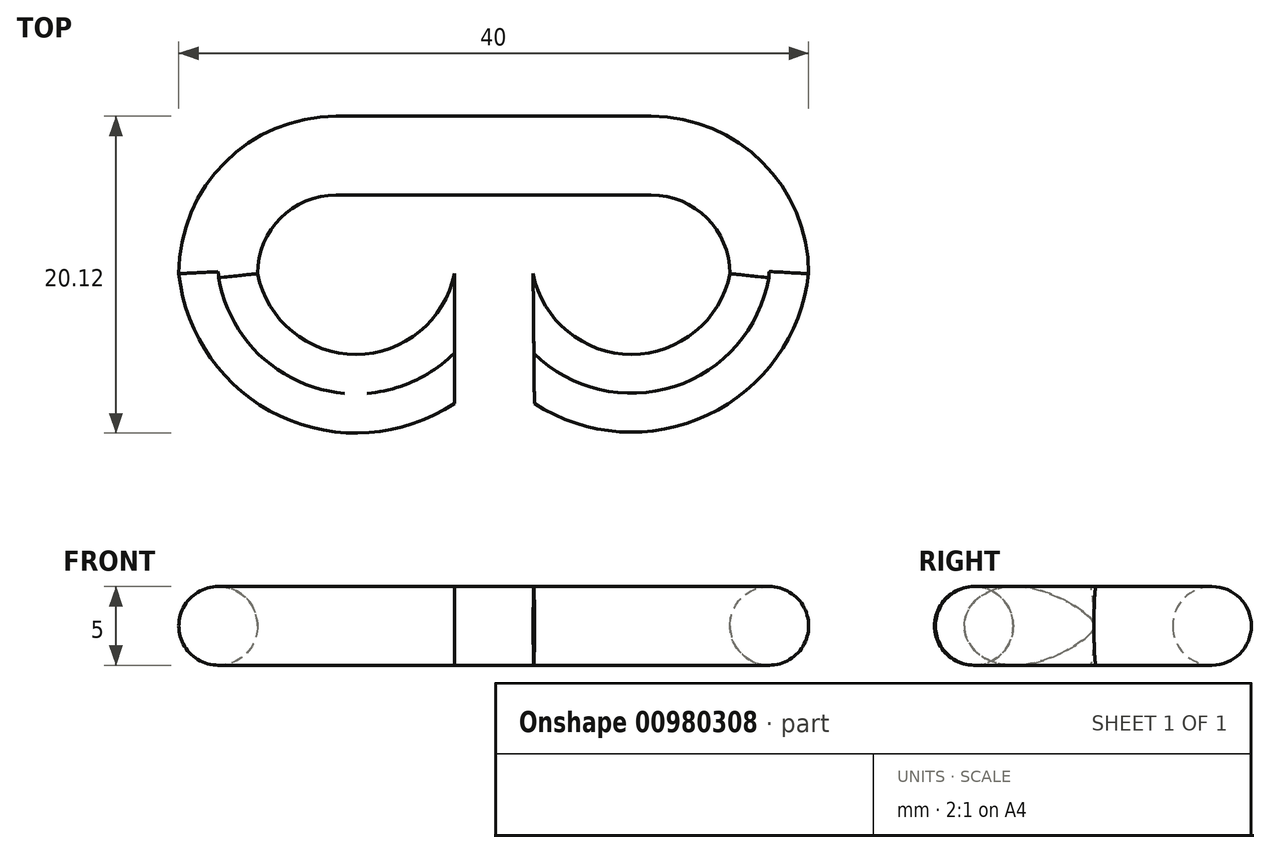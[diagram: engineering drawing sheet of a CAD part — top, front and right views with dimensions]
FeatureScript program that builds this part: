
annotation { "Feature Type Name" : "Feature", "Feature Type Description" : "" }
export const myFeature = defineFeature(function(context is Context, id is Id, definition is map)
    precondition{}
    {
        {
            var Q0;
            Q0=qCreatedBy(makeId("Top.planeOp"),FACE);
            var sketch = newSketch(context, id + "F0", { "sketchPlane" : qUnion([Q0])});
            skLineSegment(sketch, "E0.top", {"start": v(10, 5) * mm, "end": v(-10, 5) * mm});
            skLineSegment(sketch, "E0.left", {"start": v(15, 0) * mm, "end": v(15, 0) * mm});
            skLineSegment(sketch, "E0.right", {"start": v(-15, 0) * mm, "end": v(-15, 0) * mm});
            skPoint(sketch, "E0.middle", {"position": v(0, 0) * mm});
            skLineSegment(sketch, "E1.top", {"start": v(10, 10) * mm, "end": v(-10, 10) * mm});
            skLineSegment(sketch, "E1.left", {"start": v(20, 0) * mm, "end": v(20, 0) * mm});
            skLineSegment(sketch, "E1.right", {"start": v(-20, 0) * mm, "end": v(-20, 0) * mm});
            skPoint(sketch, "E2.visualSharp", {"position": v(-20, 10) * mm});
            skArc(sketch, "E2.filletArc", {"start": v(-10, 10) * mm, "mid": v(-17.07, 7.07) * mm, "end": v(-20, 0) * mm});
            skPoint(sketch, "E3.visualSharp", {"position": v(-20, -10) * mm});
            skPoint(sketch, "E4.visualSharp", {"position": v(20, 10) * mm});
            skArc(sketch, "E4.filletArc", {"start": v(20, 0) * mm, "mid": v(17.07, 7.07) * mm, "end": v(10, 10) * mm});
            skPoint(sketch, "E5.visualSharp", {"position": v(20, -10) * mm});
            skPoint(sketch, "E6.visualSharp", {"position": v(-15, -5) * mm});
            skArc(sketch, "E7.filletArc", {"start": v(-10, 5) * mm, "mid": v(-13.54, 3.54) * mm, "end": v(-15, 0) * mm});
            skPoint(sketch, "E8.visualSharp", {"position": v(15, 5) * mm});
            skArc(sketch, "E8.filletArc", {"start": v(15, 0) * mm, "mid": v(13.54, 3.54) * mm, "end": v(10, 5) * mm});
            skPoint(sketch, "E9.visualSharp", {"position": v(15, -5) * mm});
            skLineSegment(sketch, "E10.top", {"start": v(2.5, 5) * mm, "end": v(-2.5, 5) * mm});
            skArc(sketch, "E11", {"start": v(-15, 0) * mm, "mid": v(-8.75, -5.12) * mm, "end": v(-2.5, 0) * mm});
            skArc(sketch, "E12", {"start": v(-20, 0) * mm, "mid": v(-13.57, -9.05) * mm, "end": v(-2.5, -8.24) * mm});
            skArc(sketch, "E13", {"start": v(2.58, -8.24) * mm, "mid": v(13.6, -8.98) * mm, "end": v(20, 0) * mm});
            skArc(sketch, "E14", {"start": v(2.5, 0) * mm, "mid": v(8.75, -5.12) * mm, "end": v(15, 0) * mm});
            skLineSegment(sketch, "E15", {"start": v(-2.5, 0) * mm, "end": v(-2.5, -8.24) * mm});
            skLineSegment(sketch, "E16", {"start": v(2.58, -8.24) * mm, "end": v(2.5, 0) * mm});
            skSolve(sketch);
        }
        {
            var Q0;
            Q0=makeQuery(id+"F0.imprint","IMPRINT",FACE,{"disambiguationData":[TD([[makeQuery(id+"F0.imprint","IMPRINT",EDGE,{"derivedFrom":sQuery(id+"F0.wireOp",EDGE,"E1.top")}),1.0]])]});
            extrude(context, id + "F1", {"entities" : qUnion([Q0]), "depth" : 5 * mm, "offsetDistance" : 25 * mm});
        }
        {
            var Q0;
            Q0=makeQuery(id+"F1.opExtrude","CAP_EDGE",EDGE,{"disambiguationData":[OSD([sQuery(id+"F0.wireOp",EDGE,"E12")])],"isStart":false});
            var Q1;
            Q1=makeQuery(id+"F1.opExtrude","CAP_EDGE",EDGE,{"disambiguationData":[OSD([sQuery(id+"F0.wireOp",EDGE,"E2.filletArc")])],"isStart":false});
            var Q2;
            Q2=makeQuery(id+"F1.opExtrude","CAP_EDGE",EDGE,{"disambiguationData":[OSD([sQuery(id+"F0.wireOp",EDGE,"E1.top")])],"isStart":false});
            var Q3;
            Q3=makeQuery(id+"F1.opExtrude","CAP_EDGE",EDGE,{"disambiguationData":[OSD([sQuery(id+"F0.wireOp",EDGE,"E4.filletArc")])],"isStart":false});
            var Q4;
            Q4=makeQuery(id+"F1.opExtrude","CAP_EDGE",EDGE,{"disambiguationData":[OSD([sQuery(id+"F0.wireOp",EDGE,"E13")])],"isStart":false});
            var Q5;
            Q5=makeQuery(id+"F1.opExtrude","CAP_EDGE",EDGE,{"disambiguationData":[OSD([sQuery(id+"F0.wireOp",EDGE,"E14")])],"isStart":false});
            var Q6;
            Q6=makeQuery(id+"F1.opExtrude","CAP_EDGE",EDGE,{"disambiguationData":[OSD([sQuery(id+"F0.wireOp",EDGE,"E8.filletArc")])],"isStart":false});
            var Q7;
            Q7=makeQuery(id+"F1.opExtrude","CAP_EDGE",EDGE,{"disambiguationData":[OSD([sQuery(id+"F0.wireOp",EDGE,"E0.top"),sQuery(id+"F0.wireOp",EDGE,"E10.top")])],"isStart":false});
            var Q8;
            Q8=makeQuery(id+"F1.opExtrude","CAP_EDGE",EDGE,{"disambiguationData":[OSD([sQuery(id+"F0.wireOp",EDGE,"E11")])],"isStart":false});
            var Q9;
            Q9=makeQuery(id+"F1.opExtrude","CAP_EDGE",EDGE,{"disambiguationData":[OSD([sQuery(id+"F0.wireOp",EDGE,"E7.filletArc")])],"isStart":false});
            fillet(context, id + "F2", {"entities" : qUnion([Q0, Q1, Q2, Q3, Q4, Q5, Q6, Q7, Q8, Q9]), "radius" : 2.5 * mm, "allowEdgeOverflow" : false});
        }
        {
            var Q0;
            Q0=makeQuery(id+"F1.opExtrude","CAP_EDGE",EDGE,{"disambiguationData":[OSD([sQuery(id+"F0.wireOp",EDGE,"E4.filletArc")])],"isStart":true});
            var Q1;
            Q1=makeQuery(id+"F1.opExtrude","CAP_EDGE",EDGE,{"disambiguationData":[OSD([sQuery(id+"F0.wireOp",EDGE,"E13")])],"isStart":true});
            var Q2;
            Q2=makeQuery(id+"F1.opExtrude","CAP_EDGE",EDGE,{"disambiguationData":[OSD([sQuery(id+"F0.wireOp",EDGE,"E14")])],"isStart":true});
            var Q3;
            Q3=makeQuery(id+"F1.opExtrude","CAP_EDGE",EDGE,{"disambiguationData":[OSD([sQuery(id+"F0.wireOp",EDGE,"E8.filletArc")])],"isStart":true});
            var Q4;
            Q4=makeQuery(id+"F1.opExtrude","CAP_EDGE",EDGE,{"disambiguationData":[OSD([sQuery(id+"F0.wireOp",EDGE,"E0.top"),sQuery(id+"F0.wireOp",EDGE,"E10.top")])],"isStart":true});
            var Q5;
            Q5=makeQuery(id+"F1.opExtrude","CAP_EDGE",EDGE,{"disambiguationData":[OSD([sQuery(id+"F0.wireOp",EDGE,"E1.top")])],"isStart":true});
            var Q6;
            Q6=makeQuery(id+"F1.opExtrude","CAP_EDGE",EDGE,{"disambiguationData":[OSD([sQuery(id+"F0.wireOp",EDGE,"E2.filletArc")])],"isStart":true});
            var Q7;
            Q7=makeQuery(id+"F1.opExtrude","CAP_EDGE",EDGE,{"disambiguationData":[OSD([sQuery(id+"F0.wireOp",EDGE,"E11")])],"isStart":true});
            var Q8;
            Q8=makeQuery(id+"F1.opExtrude","CAP_EDGE",EDGE,{"disambiguationData":[OSD([sQuery(id+"F0.wireOp",EDGE,"E12")])],"isStart":true});
            fillet(context, id + "F3", {"entities" : qUnion([Q0, Q1, Q2, Q3, Q4, Q5, Q6, Q7, Q8]), "radius" : 2.5 * mm, "tangentPropagation" : true, "allowEdgeOverflow" : false});
        }
    });
